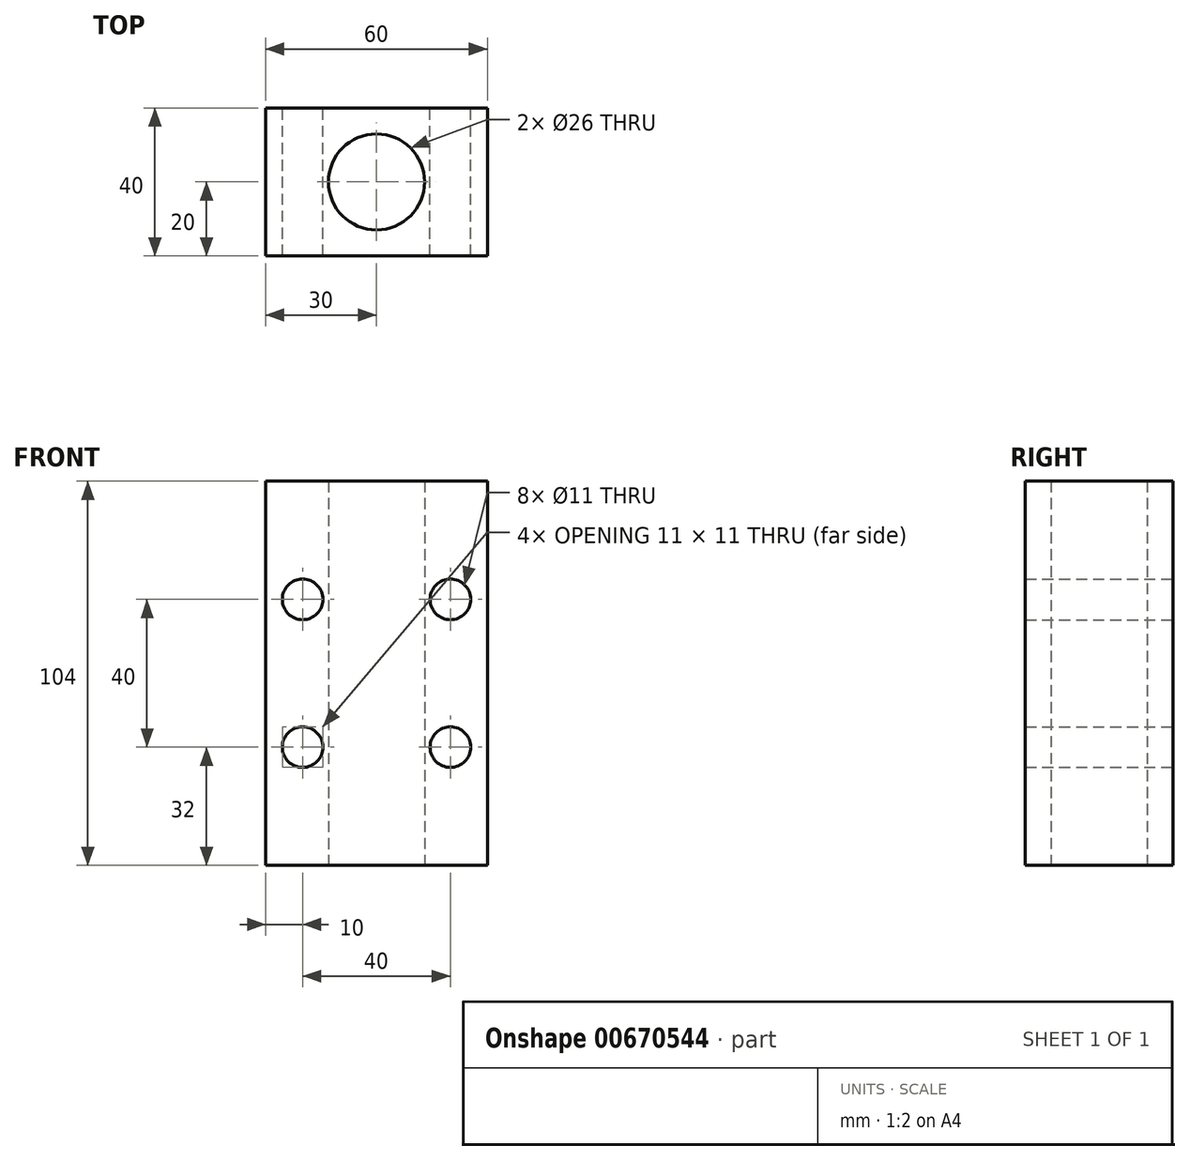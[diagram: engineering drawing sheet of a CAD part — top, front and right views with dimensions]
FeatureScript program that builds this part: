
annotation { "Feature Type Name" : "Feature", "Feature Type Description" : "" }
export const myFeature = defineFeature(function(context is Context, id is Id, definition is map)
    precondition{}
    {
        {
            var Q0;
            Q0=qCreatedBy(makeId("Front.planeOp"),FACE);
            var sketch = newSketch(context, id + "F0", { "sketchPlane" : qUnion([Q0])});
            skLineSegment(sketch, "E0.bottom", {"start": v(-30, 52) * mm, "end": v(30, 52) * mm});
            skLineSegment(sketch, "E0.top", {"start": v(-30, -52) * mm, "end": v(30, -52) * mm});
            skLineSegment(sketch, "E0.left", {"start": v(-30, 52) * mm, "end": v(-30, -52) * mm});
            skLineSegment(sketch, "E0.right", {"start": v(30, 52) * mm, "end": v(30, -52) * mm});
            skSolve(sketch);
        }
        {
            var Q0;
            Q0=makeQuery(id+"F0.imprint","IMPRINT",FACE,{"disambiguationData":[TD([[makeQuery(id+"F0.imprint","IMPRINT",EDGE,{"derivedFrom":sQuery(id+"F0.wireOp",EDGE,"E0.bottom")}),-1.0]])]});
            extrude(context, id + "F1", {"entities" : qUnion([Q0]), "depth" : 40 * mm, "offsetDistance" : 25 * mm});
        }
        {
            var Q0;
            Q0=makeQuery(id+"F1.opExtrude","SWEPT_FACE",FACE,{"disambiguationData":[OSD([sQuery(id+"F0.wireOp",EDGE,"E0.bottom")])]});
            var sketch = newSketch(context, id + "F2", { "sketchPlane" : qUnion([Q0])});
            skPoint(sketch, "E1", {"position": v(0, -20) * mm});
            skSolve(sketch);
        }
        {
            var Q0;
            Q0=sQuery(id+"F2.wireOp",VERTEX,"E1");
            var Q1;
            Q1=makeQuery(id+"F1.opExtrude","SWEPT_BODY",BODY,{"disambiguationData":[OSD([sQuery(id+"F0.wireOp",EDGE,"E0.bottom"),sQuery(id+"F0.wireOp",EDGE,"E0.top"),sQuery(id+"F0.wireOp",EDGE,"E0.left"),sQuery(id+"F0.wireOp",EDGE,"E0.right")])]});
            hole(context, id + "F3", {"style" : HoleStyle.SIMPLE, "endStyle" : HoleEndStyle.BLIND, "standardTappedOrClearance" : lookupTablePath({ "fit" : "Normal", "standard" : "ISO", "size" : "M24", "type" : "Clearance" }), "standardBlindInLast" : lookupTablePath({ "fit" : "Normal", "standard" : "ISO", "engagement" : "75%", "pitch" : "2 mm", "size" : "M24", "type" : "Clearance & tapped" }), "holeDiameter" : 26 * mm, "majorDiameter" : 5 * mm, "holeDepth" : 104 * mm, "isTappedThrough" : true, "tappedDepth" : 15 * mm, "tapClearance" : 3, "locations" : qUnion([Q0]), "scope" : qUnion([Q1]), "startStyle" : HoleStartStyle.PART});
        }
        {
            var Q0;
            Q0=makeQuery(id+"F1.opExtrude","CAP_FACE",FACE,{"disambiguationData":[OSD([sQuery(id+"F0.wireOp",EDGE,"E0.bottom"),sQuery(id+"F0.wireOp",EDGE,"E0.top"),sQuery(id+"F0.wireOp",EDGE,"E0.left"),sQuery(id+"F0.wireOp",EDGE,"E0.right")])],"isStart":false});
            var sketch = newSketch(context, id + "F4", { "sketchPlane" : qUnion([Q0])});
            skPoint(sketch, "E2", {"position": v(-20, 20) * mm});
            skPoint(sketch, "E3", {"position": v(-20, -20) * mm});
            skPoint(sketch, "E4", {"position": v(20, 20) * mm});
            skPoint(sketch, "E5", {"position": v(20, -20) * mm});
            skSolve(sketch);
        }
        {
            var Q0;
            Q0=sQuery(id+"F4.wireOp",VERTEX,"E2");
            var Q1;
            Q1=sQuery(id+"F4.wireOp",VERTEX,"E3");
            var Q2;
            Q2=sQuery(id+"F4.wireOp",VERTEX,"E5");
            var Q3;
            Q3=sQuery(id+"F4.wireOp",VERTEX,"E4");
            var Q4;
            Q4=makeQuery(id+"F1.opExtrude","SWEPT_BODY",BODY,{"disambiguationData":[OSD([sQuery(id+"F0.wireOp",EDGE,"E0.bottom"),sQuery(id+"F0.wireOp",EDGE,"E0.top"),sQuery(id+"F0.wireOp",EDGE,"E0.left"),sQuery(id+"F0.wireOp",EDGE,"E0.right")])]});
            hole(context, id + "F5", {"style" : HoleStyle.SIMPLE, "endStyle" : HoleEndStyle.BLIND, "standardTappedOrClearance" : lookupTablePath({ "fit" : "Normal", "standard" : "ISO", "size" : "M10", "type" : "Clearance" }), "standardBlindInLast" : lookupTablePath({ "fit" : "Normal", "standard" : "ISO", "engagement" : "75%", "pitch" : "1.5 mm", "size" : "M10", "type" : "Clearance & tapped" }), "holeDiameter" : 11 * mm, "majorDiameter" : 5 * mm, "holeDepth" : 104 * mm, "isTappedThrough" : true, "tappedDepth" : 15 * mm, "tapClearance" : 3, "locations" : qUnion([Q0, Q1, Q2, Q3]), "scope" : qUnion([Q4]), "startStyle" : HoleStartStyle.PART});
        }
    });
